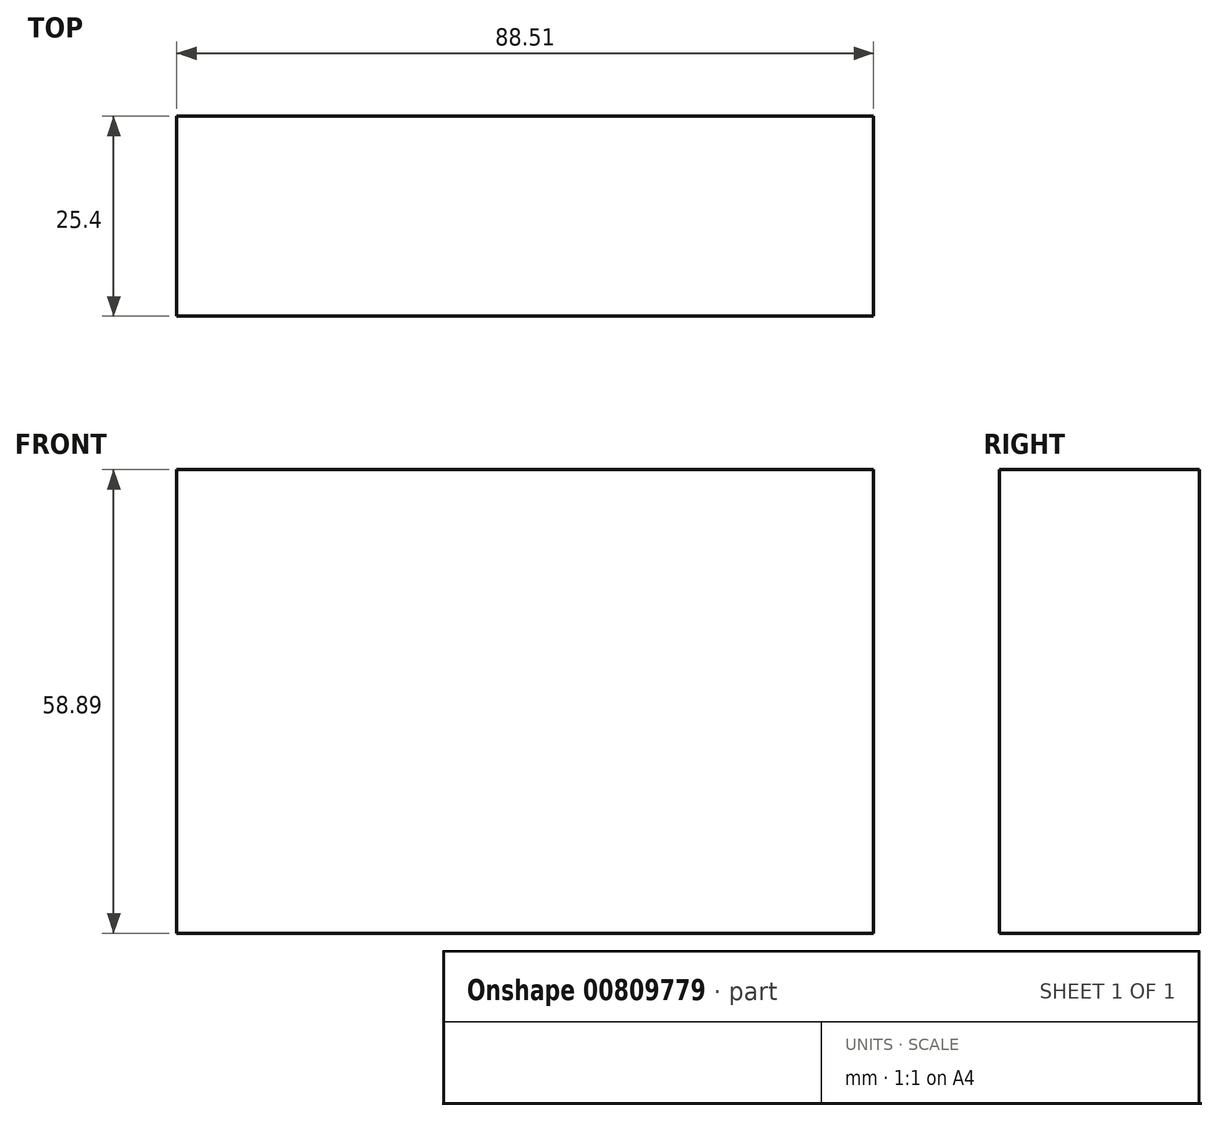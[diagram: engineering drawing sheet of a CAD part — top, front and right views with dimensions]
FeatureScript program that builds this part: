
annotation { "Feature Type Name" : "Feature", "Feature Type Description" : "" }
export const myFeature = defineFeature(function(context is Context, id is Id, definition is map)
    precondition{}
    {
        {
            var Q0;
            Q0=qCreatedBy(makeId("Front.planeOp"),FACE);
            var sketch = newSketch(context, id + "F0", { "sketchPlane" : qUnion([Q0])});
            skLineSegment(sketch, "E0.bottom", {"start": v(-60.36, 29.88) * mm, "end": v(28.15, 29.88) * mm});
            skLineSegment(sketch, "E0.top", {"start": v(-60.36, -29) * mm, "end": v(28.15, -29) * mm});
            skLineSegment(sketch, "E0.left", {"start": v(-60.36, 29.88) * mm, "end": v(-60.36, -29) * mm});
            skLineSegment(sketch, "E0.right", {"start": v(28.15, 29.88) * mm, "end": v(28.15, -29) * mm});
            skSolve(sketch);
        }
        {
            var Q0;
            Q0=makeQuery(id+"F0.imprint","IMPRINT",FACE,{"disambiguationData":[TD([[makeQuery(id+"F0.imprint","IMPRINT",EDGE,{"derivedFrom":sQuery(id+"F0.wireOp",EDGE,"E0.bottom")}),-1.0]])]});
            extrude(context, id + "F1", {"entities" : qUnion([Q0]), "depth" : 25.4 * mm, "offsetDistance" : 25.4 * mm});
        }
    });
